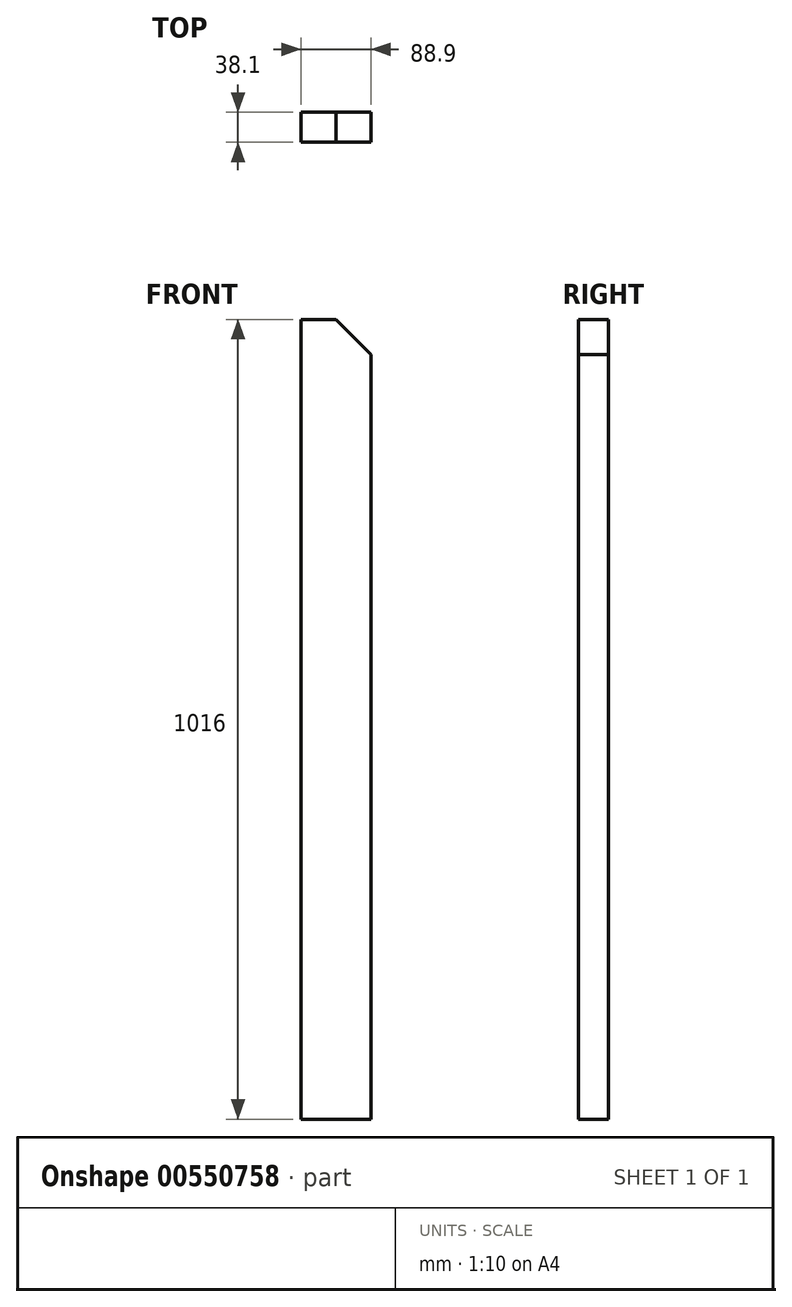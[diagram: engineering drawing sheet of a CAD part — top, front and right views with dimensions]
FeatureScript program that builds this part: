
annotation { "Feature Type Name" : "Feature", "Feature Type Description" : "" }
export const myFeature = defineFeature(function(context is Context, id is Id, definition is map)
    precondition{}
    {
        {
            var Q0;
            Q0=qCreatedBy(makeId("Front.planeOp"),FACE);
            var sketch = newSketch(context, id + "F0", { "sketchPlane" : qUnion([Q0])});
            skLineSegment(sketch, "E0", {"start": v(0, 0) * mm, "end": v(88.9, 0) * mm});
            skLineSegment(sketch, "E1", {"start": v(88.9, 0) * mm, "end": v(88.9, 971.55) * mm});
            skLineSegment(sketch, "E2", {"start": v(88.9, 971.55) * mm, "end": v(44.45, 1016) * mm});
            skLineSegment(sketch, "E3", {"start": v(0, 1016) * mm, "end": v(0, 0) * mm});
            skLineSegment(sketch, "E4", {"start": v(0, 1016) * mm, "end": v(44.45, 1016) * mm});
            skPoint(sketch, "E5.orphan", {"position": v(0, 1060.45) * mm});
            skSolve(sketch);
        }
        {
            var Q0;
            Q0=makeQuery(id+"F0.imprint","IMPRINT",FACE,{"disambiguationData":[TD([[makeQuery(id+"F0.imprint","IMPRINT",EDGE,{"derivedFrom":sQuery(id+"F0.wireOp",EDGE,"E0")}),1.0]])]});
            var Q1;
            Q1=qConstructionFilter(qBodyType(qCreatedBy(id+"F0",EDGE),BodyType.WIRE),ConstructionObject.NO);
            extrude(context, id + "F1", {"entities" : qUnion([Q0]), "surfaceEntities" : qUnion([Q1]), "oppositeDirection" : true, "depth" : 38.1 * mm, "offsetDistance" : 25.4 * mm});
        }
    });
